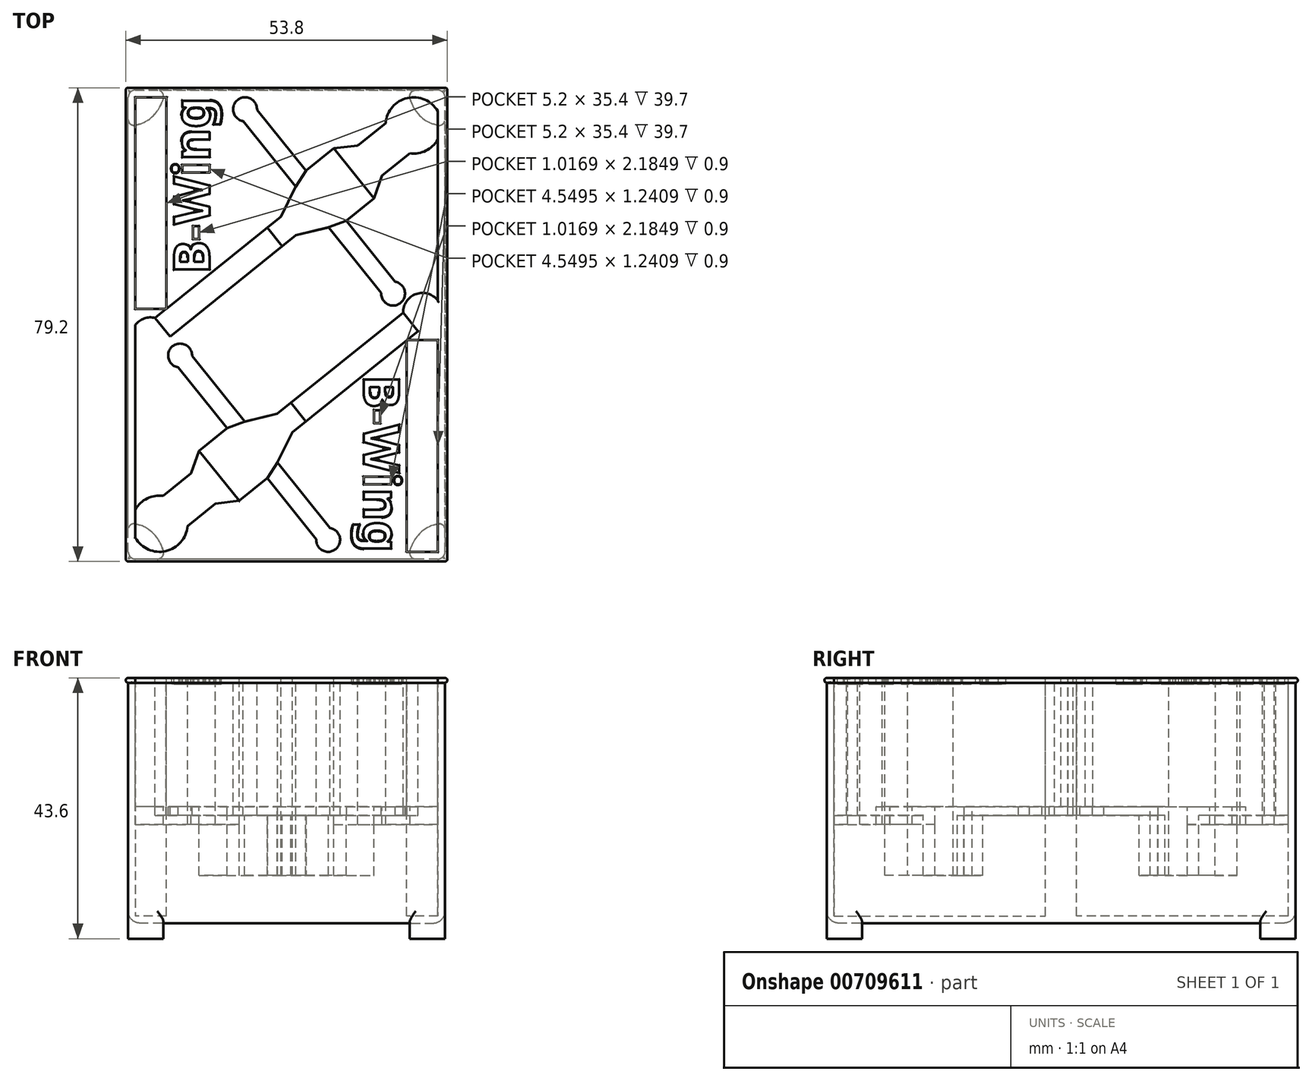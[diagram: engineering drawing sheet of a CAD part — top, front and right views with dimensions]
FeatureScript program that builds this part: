
annotation { "Feature Type Name" : "Feature", "Feature Type Description" : "" }
export const myFeature = defineFeature(function(context is Context, id is Id, definition is map)
    precondition{}
    {
        {
            var Q0;
            Q0=qCreatedBy(makeId("Front.planeOp"),FACE);
            var sketch = newSketch(context, id + "F0", { "sketchPlane" : qUnion([Q0])});
            skLineSegment(sketch, "E0.bottom", {"start": v(26.5, 20.5) * mm, "end": v(-26.5, 20.5) * mm});
            skLineSegment(sketch, "E0.top", {"start": v(26.5, -20.5) * mm, "end": v(-26.5, -20.5) * mm});
            skLineSegment(sketch, "E0.left", {"start": v(26.5, 20.5) * mm, "end": v(26.5, -20.5) * mm});
            skLineSegment(sketch, "E0.right", {"start": v(-26.5, 20.5) * mm, "end": v(-26.5, -20.5) * mm});
            skPoint(sketch, "E0.middle", {"position": v(0, 0) * mm});
            skSolve(sketch);
        }
        {
            var Q0;
            Q0=makeQuery(id+"F0.imprint","IMPRINT",FACE,{"disambiguationData":[TD([[makeQuery(id+"F0.imprint","IMPRINT",EDGE,{"derivedFrom":sQuery(id+"F0.wireOp",EDGE,"E0.bottom")}),1.0]])]});
            extrude(context, id + "F1", {"entities" : qUnion([Q0]), "depth" : 78.4 * mm, "offsetDistance" : 25 * mm, "symmetric" : true});
        }
        {
            var Q0;
            Q0=makeQuery(id+"F1.opExtrude","SWEPT_FACE",FACE,{"disambiguationData":[OSD([sQuery(id+"F0.wireOp",EDGE,"E0.bottom")])]});
            shell(context, id + "F2", {"entities" : qUnion([Q0]), "thickness" : 1.2 * mm});
        }
        {
            var Q0;
            Q0=makeQuery(id+"F1.opExtrude","SWEPT_FACE",FACE,{"disambiguationData":[OSD([sQuery(id+"F0.wireOp",EDGE,"E0.top")])]});
            var sketch = newSketch(context, id + "F3", { "sketchPlane" : qUnion([Q0])});
            skArc(sketch, "E1", {"start": v(20.62, 38) * mm, "mid": v(22.26, 34.96) * mm, "end": v(25.3, 33.32) * mm});
            skLineSegment(sketch, "E2", {"start": v(26.5, 39.2) * mm, "end": v(21.6, 39.2) * mm});
            skLineSegment(sketch, "E3", {"start": v(26.5, 39.2) * mm, "end": v(26.5, 34.3) * mm});
            skPoint(sketch, "E4.visualSharp", {"position": v(20.5, 39.2) * mm});
            skArc(sketch, "E4.filletArc", {"start": v(21.6, 39.2) * mm, "mid": v(20.83, 38.83) * mm, "end": v(20.62, 38) * mm});
            skPoint(sketch, "E5.visualSharp", {"position": v(26.5, 33.2) * mm});
            skArc(sketch, "E5.filletArc", {"start": v(25.3, 33.32) * mm, "mid": v(26.13, 33.53) * mm, "end": v(26.5, 34.3) * mm});
            skArc(sketch, "E6.MirrorCS", {"start": v(-25.3, 33.32) * mm, "mid": v(-26.13, 33.53) * mm, "end": v(-26.5, 34.3) * mm});
            skArc(sketch, "E7.MirrorCS", {"start": v(-21.6, 39.2) * mm, "mid": v(-20.83, 38.83) * mm, "end": v(-20.62, 38) * mm});
            skPoint(sketch, "E8.MirrorP", {"position": v(-20.5, 39.2) * mm});
            skArc(sketch, "E9.MirrorCS", {"start": v(-20.62, 38) * mm, "mid": v(-22.26, 34.96) * mm, "end": v(-25.3, 33.32) * mm});
            skLineSegment(sketch, "E10.MirrorCS", {"start": v(-26.5, 39.2) * mm, "end": v(-21.6, 39.2) * mm});
            skLineSegment(sketch, "E11.MirrorCS", {"start": v(-26.5, 39.2) * mm, "end": v(-26.5, 34.3) * mm});
            skPoint(sketch, "E12.MirrorP", {"position": v(-26.5, 33.2) * mm});
            skArc(sketch, "E13.MirrorCS", {"start": v(25.3, -33.32) * mm, "mid": v(26.13, -33.53) * mm, "end": v(26.5, -34.3) * mm});
            skArc(sketch, "E14.MirrorCS", {"start": v(21.6, -39.2) * mm, "mid": v(20.83, -38.83) * mm, "end": v(20.62, -38) * mm});
            skArc(sketch, "E15.MirrorCS", {"start": v(-25.3, -33.32) * mm, "mid": v(-26.13, -33.53) * mm, "end": v(-26.5, -34.3) * mm});
            skArc(sketch, "E16.MirrorCS", {"start": v(-21.6, -39.2) * mm, "mid": v(-20.83, -38.83) * mm, "end": v(-20.62, -38) * mm});
            skPoint(sketch, "E17.MirrorP", {"position": v(-26.5, -33.2) * mm});
            skPoint(sketch, "E18.MirrorP", {"position": v(20.5, -39.2) * mm});
            skPoint(sketch, "E19.MirrorP", {"position": v(26.5, -33.2) * mm});
            skLineSegment(sketch, "E20.MirrorCS", {"start": v(-26.5, -39.2) * mm, "end": v(-26.5, -34.3) * mm});
            skPoint(sketch, "E21.MirrorP", {"position": v(-20.5, -39.2) * mm});
            skLineSegment(sketch, "E22.MirrorCS", {"start": v(26.5, -39.2) * mm, "end": v(26.5, -34.3) * mm});
            skLineSegment(sketch, "E23.MirrorCS", {"start": v(-26.5, -39.2) * mm, "end": v(-21.6, -39.2) * mm});
            skLineSegment(sketch, "E24.MirrorCS", {"start": v(26.5, -39.2) * mm, "end": v(21.6, -39.2) * mm});
            skArc(sketch, "E25.MirrorCS", {"start": v(20.62, -38) * mm, "mid": v(22.26, -34.96) * mm, "end": v(25.3, -33.32) * mm});
            skArc(sketch, "E26.MirrorCS", {"start": v(-20.62, -38) * mm, "mid": v(-22.26, -34.96) * mm, "end": v(-25.3, -33.32) * mm});
            skSolve(sketch);
        }
        {
            var Q0;
            Q0=qSketchRegion(id+"F3",true);
            extrude(context, id + "F4", {"entities" : qUnion([Q0]), "operationType" : NewBodyOperationType.ADD, "depth" : 2.6 * mm, "offsetDistance" : 25 * mm});
        }
        {
            var Q0;
            Q0=makeQuery(id+"F4.boolean.opBoolean","MERGE",FACE,{"derivedFrom":[makeQuery(id+"F1.opExtrude","CAP_FACE",FACE,{"disambiguationData":[OSD([sQuery(id+"F0.wireOp",EDGE,"E0.bottom"),sQuery(id+"F0.wireOp",EDGE,"E0.top"),sQuery(id+"F0.wireOp",EDGE,"E0.left"),sQuery(id+"F0.wireOp",EDGE,"E0.right")])],"isStart":false}),makeQuery(id+"F4.opExtrude","SWEPT_FACE",FACE,{"disambiguationData":[OSD([sQuery(id+"F3.wireOp",EDGE,"E2")])]}),makeQuery(id+"F4.opExtrude","SWEPT_FACE",FACE,{"disambiguationData":[OSD([sQuery(id+"F3.wireOp",EDGE,"E10.MirrorCS")])]})]});
            var sketch = newSketch(context, id + "F5", { "sketchPlane" : qUnion([Q0])});
            skLineSegment(sketch, "E27", {"start": v(-26.5, 20.5) * mm, "end": v(-26.5, 19.7) * mm});
            skArc(sketch, "E28", {"start": v(-26.5, 20.5) * mm, "mid": v(-26.9, 20.1) * mm, "end": v(-26.5, 19.7) * mm});
            skSolve(sketch);
        }
        {
            var Q0;
            Q0=makeQuery(id+"F5.imprint","IMPRINT",FACE,{"disambiguationData":[TD([[makeQuery(id+"F5.imprint","IMPRINT",EDGE,{"derivedFrom":sQuery(id+"F5.wireOp",EDGE,"E27")}),-1.0]])]});
            var Q1;
            Q1=makeQuery(id+"F1.opExtrude","SWEPT_EDGE",EDGE,{"disambiguationData":[OSD([sQuery(id+"F0.wireOp",EDGE,"E0.bottom"),sQuery(id+"F0.wireOp",EDGE,"E0.right")])]});
            var Q2;
            Q2=makeQuery(id+"F1.opExtrude","CAP_EDGE",EDGE,{"disambiguationData":[OSD([sQuery(id+"F0.wireOp",EDGE,"E0.bottom")])],"isStart":false});
            var Q3;
            Q3=makeQuery(id+"F1.opExtrude","SWEPT_EDGE",EDGE,{"disambiguationData":[OSD([sQuery(id+"F0.wireOp",EDGE,"E0.bottom"),sQuery(id+"F0.wireOp",EDGE,"E0.left")])]});
            var Q4;
            Q4=makeQuery(id+"F1.opExtrude","CAP_EDGE",EDGE,{"disambiguationData":[OSD([sQuery(id+"F0.wireOp",EDGE,"E0.bottom")])],"isStart":true});
            sweep(context, id + "F6", {"operationType" : NewBodyOperationType.ADD, "profiles" : qUnion([Q0]), "path" : qUnion([Q1, Q2, Q3, Q4])});
        }
        {
            var Q0;
            Q0=makeQuery(id+"F1.opExtrude","CAP_EDGE",EDGE,{"disambiguationData":[OSD([sQuery(id+"F0.wireOp",EDGE,"E0.top")])],"isStart":false});
            var Q1;
            Q1=makeQuery(id+"F1.opExtrude","SWEPT_EDGE",EDGE,{"disambiguationData":[OSD([sQuery(id+"F0.wireOp",EDGE,"E0.top"),sQuery(id+"F0.wireOp",EDGE,"E0.left")])]});
            var Q2;
            Q2=makeQuery(id+"F1.opExtrude","SWEPT_EDGE",EDGE,{"disambiguationData":[OSD([sQuery(id+"F0.wireOp",EDGE,"E0.top"),sQuery(id+"F0.wireOp",EDGE,"E0.right")])]});
            var Q3;
            Q3=makeQuery(id+"F1.opExtrude","CAP_EDGE",EDGE,{"disambiguationData":[OSD([sQuery(id+"F0.wireOp",EDGE,"E0.top")])],"isStart":true});
            fillet(context, id + "F7", {"entities" : qUnion([Q0, Q1, Q2, Q3]), "radius" : 2 * mm, "tangentPropagation" : true, "allowEdgeOverflow" : false});
        }
        {
            var Q0;
            Q0=makeQuery(id+"F4.boolean.opBoolean","MERGE",EDGE,{"derivedFrom":[makeQuery(id+"F1.opExtrude","CAP_EDGE",EDGE,{"disambiguationData":[OSD([sQuery(id+"F0.wireOp",EDGE,"E0.right")])],"isStart":false}),makeQuery(id+"F4.opExtrude","SWEPT_EDGE",EDGE,{"disambiguationData":[OSD([sQuery(id+"F3.wireOp",EDGE,"E10.MirrorCS"),sQuery(id+"F3.wireOp",EDGE,"E11.MirrorCS")])]})]});
            var Q1;
            Q1=makeQuery(id+"F4.boolean.opBoolean","MERGE",EDGE,{"derivedFrom":[makeQuery(id+"F1.opExtrude","CAP_EDGE",EDGE,{"disambiguationData":[OSD([sQuery(id+"F0.wireOp",EDGE,"E0.left")])],"isStart":false}),makeQuery(id+"F4.opExtrude","SWEPT_EDGE",EDGE,{"disambiguationData":[OSD([sQuery(id+"F3.wireOp",EDGE,"E2"),sQuery(id+"F3.wireOp",EDGE,"E3")])]})]});
            var Q2;
            Q2=makeQuery(id+"F4.boolean.opBoolean","MERGE",EDGE,{"derivedFrom":[makeQuery(id+"F1.opExtrude","CAP_EDGE",EDGE,{"disambiguationData":[OSD([sQuery(id+"F0.wireOp",EDGE,"E0.left")])],"isStart":true}),makeQuery(id+"F4.opExtrude","SWEPT_EDGE",EDGE,{"disambiguationData":[OSD([sQuery(id+"F3.wireOp",EDGE,"E22.MirrorCS"),sQuery(id+"F3.wireOp",EDGE,"E24.MirrorCS")])]})]});
            var Q3;
            Q3=makeQuery(id+"F4.boolean.opBoolean","MERGE",EDGE,{"derivedFrom":[makeQuery(id+"F1.opExtrude","CAP_EDGE",EDGE,{"disambiguationData":[OSD([sQuery(id+"F0.wireOp",EDGE,"E0.right")])],"isStart":true}),makeQuery(id+"F4.opExtrude","SWEPT_EDGE",EDGE,{"disambiguationData":[OSD([sQuery(id+"F3.wireOp",EDGE,"E20.MirrorCS"),sQuery(id+"F3.wireOp",EDGE,"E23.MirrorCS")])]})]});
            fillet(context, id + "F8", {"entities" : qUnion([Q0, Q1, Q2, Q3]), "radius" : 1.2 * mm, "tangentPropagation" : true, "allowEdgeOverflow" : false});
        }
        {
            var Q0;
            Q0=makeQuery(id+"F6.opSweep","MID_CAP_EDGE",EDGE,{"disambiguationData":[OSD([sQuery(id+"F0.wireOp",EDGE,"E0.bottom"),sQuery(id+"F0.wireOp",EDGE,"E0.right"),sQuery(id+"F5.wireOp",EDGE,"E28")])],"capPos":1.0});
            var Q1;
            Q1=makeQuery(id+"F6.opSweep","CAP_EDGE",EDGE,{"disambiguationData":[OSD([sQuery(id+"F0.wireOp",EDGE,"E0.bottom"),sQuery(id+"F0.wireOp",EDGE,"E0.right"),sQuery(id+"F5.wireOp",EDGE,"E28")])],"isStart":true});
            var Q2;
            Q2=makeQuery(id+"F6.opSweep","MID_CAP_EDGE",EDGE,{"disambiguationData":[OSD([sQuery(id+"F0.wireOp",EDGE,"E0.bottom"),sQuery(id+"F0.wireOp",EDGE,"E0.left"),sQuery(id+"F5.wireOp",EDGE,"E28")])],"capPos":3.0});
            var Q3;
            Q3=makeQuery(id+"F6.opSweep","MID_CAP_EDGE",EDGE,{"disambiguationData":[OSD([sQuery(id+"F0.wireOp",EDGE,"E0.bottom"),sQuery(id+"F0.wireOp",EDGE,"E0.left"),sQuery(id+"F5.wireOp",EDGE,"E28")])],"capPos":2.0});
            fillet(context, id + "F9", {"entities" : qUnion([Q0, Q1, Q2, Q3]), "radius" : .4 * mm, "tangentPropagation" : true, "allowEdgeOverflow" : false});
        }
        {
            var Q0;
            {var subQ0=sQuery(id+"F12.wireOp",EDGE,"E179.MirrorCS");var subQ1=sQuery(id+"F12.wireOp",EDGE,"E174.MirrorCS");var subQ2=sQuery(id+"F12.wireOp",EDGE,"E171.MirrorCS");var subQ3=sQuery(id+"F12.wireOp",EDGE,"E87");var subQ4=sQuery(id+"F12.wireOp",EDGE,"E86");var subQ5=sQuery(id+"F12.wireOp",EDGE,"E85.0");var subQ6=sQuery(id+"F12.wireOp",EDGE,"E83.MirrorCS");var subQ7=sQuery(id+"F12.wireOp",EDGE,"E76.MirrorCS");Q0=makeQuery(id+"F13.boolean.opBoolean","MERGE",FACE,{"derivedFrom":[makeQuery(id+"F1.opExtrude","SWEPT_FACE",FACE,{"disambiguationData":[OSD([sQuery(id+"F0.wireOp",EDGE,"E0.bottom")])]}),makeQuery(id+"F13.opExtrude","CAP_FACE",FACE,{"disambiguationData":[OSD([sQuery(id+"F12.wireOp",EDGE,"E64"),sQuery(id+"F12.wireOp",EDGE,"E65"),sQuery(id+"F12.wireOp",EDGE,"E66"),sQuery(id+"F12.wireOp",EDGE,"E67"),sQuery(id+"F12.wireOp",EDGE,"E68"),sQuery(id+"F12.wireOp",EDGE,"E69"),sQuery(id+"F12.wireOp",EDGE,"E70"),sQuery(id+"F12.wireOp",EDGE,"E71"),sQuery(id+"F12.wireOp",EDGE,"E72"),sQuery(id+"F12.wireOp",EDGE,"E73.trimOffspring"),sQuery(id+"F12.wireOp",EDGE,"E79.MirrorCS"),subQ4,subQ3,sQuery(id+"F12.wireOp",EDGE,"E161.MirrorCS"),sQuery(id+"F12.wireOp",EDGE,"E162.MirrorCS"),sQuery(id+"F12.wireOp",EDGE,"E163.MirrorCS"),sQuery(id+"F12.wireOp",EDGE,"E164.MirrorCS"),sQuery(id+"F12.wireOp",EDGE,"E168.MirrorCS"),sQuery(id+"F12.wireOp",EDGE,"E169.MirrorCS"),sQuery(id+"F12.wireOp",EDGE,"E170.MirrorCS"),sQuery(id+"F12.wireOp",EDGE,"E173.MirrorCS"),sQuery(id+"F12.wireOp",EDGE,"E177.MirrorCS"),sQuery(id+"F12.wireOp",EDGE,"E178.MirrorCS"),sQuery(id+"F12.wireOp",EDGE,"E182.MirrorCS")])],"isStart":true}),makeQuery(id+"F13.opExtrude","CAP_FACE",FACE,{"disambiguationData":[OSD([sQuery(id+"F12.wireOp",EDGE,"E74.MirrorCS"),sQuery(id+"F12.wireOp",EDGE,"E75.MirrorCS"),subQ7,sQuery(id+"F12.wireOp",EDGE,"E77.MirrorCS"),sQuery(id+"F12.wireOp",EDGE,"E82.MirrorCS"),subQ6,subQ5])],"isStart":true}),makeQuery(id+"F13.opExtrude","CAP_FACE",FACE,{"disambiguationData":[OSD([subQ7,subQ5,subQ4,sQuery(id+"F12.wireOp",EDGE,"E184.trimOffspring")])],"isStart":true}),makeQuery(id+"F13.opExtrude","CAP_FACE",FACE,{"disambiguationData":[OSD([sQuery(id+"F12.wireOp",EDGE,"E78.MirrorCS"),sQuery(id+"F12.wireOp",EDGE,"E80.MirrorCS"),sQuery(id+"F12.wireOp",EDGE,"E81.MirrorCS"),subQ6,subQ5,subQ3,sQuery(id+"F12.wireOp",EDGE,"E186.trimOffspring")])],"isStart":true}),makeQuery(id+"F13.opExtrude","CAP_FACE",FACE,{"disambiguationData":[OSD([subQ4,sQuery(id+"F12.wireOp",EDGE,"E167.MirrorCS"),subQ2,sQuery(id+"F12.wireOp",EDGE,"E175.MirrorCS"),subQ0,sQuery(id+"F12.wireOp",EDGE,"E181.MirrorCS"),sQuery(id+"F12.wireOp",EDGE,"E185.trimOffspring")])],"isStart":true}),makeQuery(id+"F13.opExtrude","CAP_FACE",FACE,{"disambiguationData":[OSD([subQ3,subQ1,subQ0,sQuery(id+"F12.wireOp",EDGE,"E187.trimOffspring")])],"isStart":true}),makeQuery(id+"F13.opExtrude","CAP_FACE",FACE,{"disambiguationData":[OSD([sQuery(id+"F12.wireOp",EDGE,"E165.MirrorCS"),sQuery(id+"F12.wireOp",EDGE,"E166.MirrorCS"),subQ2,sQuery(id+"F12.wireOp",EDGE,"E172.MirrorCS"),subQ1,sQuery(id+"F12.wireOp",EDGE,"E176.MirrorCS"),subQ0])],"isStart":true})]});}
            var sketch = newSketch(context, id + "F10", { "sketchPlane" : qUnion([Q0])});
            skLineSegment(sketch, "E29.0", {"start": v(38.64, -19.37) * mm, "end": v(38.64, 56.63) * mm});
            skLineSegment(sketch, "E30.MirrorCS", {"start": v(48.84, -19.37) * mm, "end": v(48.84, 16.03) * mm});
            skLineSegment(sketch, "E31.MirrorCS", {"start": v(48.84, 16.03) * mm, "end": v(38.64, 16.03) * mm});
            skLineSegment(sketch, "E32", {"start": v(25.3, -38) * mm, "end": v(25.3, -2.6) * mm});
            skLineSegment(sketch, "E33", {"start": v(25.3, -2.6) * mm, "end": v(20.1, -2.6) * mm});
            skLineSegment(sketch, "E34", {"start": v(20.1, -2.6) * mm, "end": v(20.1, -38) * mm});
            skLineSegment(sketch, "E35", {"start": v(20.1, -38) * mm, "end": v(25.3, -38) * mm});
            skLineSegment(sketch, "E36", {"start": v(-25.3, 38) * mm, "end": v(-20.1, 38) * mm});
            skLineSegment(sketch, "E37", {"start": v(-20.1, 38) * mm, "end": v(-20.1, 2.6) * mm});
            skLineSegment(sketch, "E38", {"start": v(-20.1, 2.6) * mm, "end": v(-25.3, 2.6) * mm});
            skLineSegment(sketch, "E39", {"start": v(-25.3, 2.6) * mm, "end": v(-25.3, 38) * mm});
            skSolve(sketch);
        }
        {
            var Q0;
            {var subQ3=sQuery(id+"F10.wireOp",EDGE,"E33");Q0=makeQuery(id+"F10.imprint","IMPRINT",FACE,{"disambiguationData":[TD([[makeQuery(id+"F10.imprint","IMPRINT",EDGE,{"derivedFrom":subQ3}),-1.0]])]});}
            var Q1;
            Q1=makeQuery(id+"F13.boolean.opBoolean","SPLIT",FACE,{"disambiguationData":[TD([makeQuery(id+"F13.opExtrude","SWEPT_FACE",FACE,{"disambiguationData":[OSD([sQuery(id+"F12.wireOp",EDGE,"E64")])]})])],"derivedFrom":makeQuery(id+"F2.opShell","OFFSET_FACE",FACE,{"disambiguationData":[OSD([sQuery(id+"F0.wireOp",EDGE,"E0.top")])]})});
            extrude(context, id + "F11", {"entities" : qUnion([Q0]), "operationType" : NewBodyOperationType.ADD, "endBound" : BoundingType.UP_TO_SURFACE, "oppositeDirection" : true, "depth" : 25 * mm, "endBoundEntityFace" : qUnion([Q1]), "offsetDistance" : 25 * mm});
        }
        {
            var Q0;
            Q0=makeQuery(id+"F1.opExtrude","SWEPT_FACE",FACE,{"disambiguationData":[OSD([sQuery(id+"F0.wireOp",EDGE,"E0.bottom")])]});
            var sketch = newSketch(context, id + "F12", { "sketchPlane" : qUnion([Q0])});
            skLineSegment(sketch, "E40", {"start": v(240.04, 16.27) * mm, "end": v(253.11, 16.27) * mm});
            skLineSegment(sketch, "E41", {"start": v(240.04, 16.27) * mm, "end": v(240.04, 22.27) * mm});
            skLineSegment(sketch, "E42", {"start": v(236.67, 8.2) * mm, "end": v(236.67, -18.8) * mm});
            skLineSegment(sketch, "E43", {"start": v(237.92, 25.66) * mm, "end": v(237.92, 31.66) * mm});
            skLineSegment(sketch, "E44", {"start": v(239.04, 13.27) * mm, "end": v(236.67, 8.2) * mm});
            skLineSegment(sketch, "E45", {"start": v(240.04, 22.27) * mm, "end": v(237.92, 25.66) * mm});
            skArc(sketch, "E46", {"start": v(234.67, -24.62) * mm, "mid": v(237.74, -22.43) * mm, "end": v(236.67, -18.8) * mm});
            skArc(sketch, "E47", {"start": v(237.92, 31.66) * mm, "mid": v(239.03, 36.8) * mm, "end": v(234.67, 39.76) * mm});
            skArc(sketch, "E48", {"start": v(253.11, 13.27) * mm, "mid": v(256.44, 14.77) * mm, "end": v(253.11, 16.27) * mm});
            skLineSegment(sketch, "E49.trimOffspring", {"start": v(253.11, 13.27) * mm, "end": v(239.04, 13.27) * mm});
            skPoint(sketch, "E50.orphan", {"position": v(237.87, -18.8) * mm});
            skPoint(sketch, "E51.start.orphan", {"position": v(237.92, 28.66) * mm});
            skLineSegment(sketch, "E52.MirrorCS", {"start": v(229.3, 22.27) * mm, "end": v(231.42, 25.66) * mm});
            skLineSegment(sketch, "E53.MirrorCS", {"start": v(231.42, 25.66) * mm, "end": v(231.42, 31.66) * mm});
            skArc(sketch, "E54.MirrorCS", {"start": v(231.42, 31.66) * mm, "mid": v(230.3, 36.8) * mm, "end": v(234.67, 39.76) * mm});
            skLineSegment(sketch, "E55.MirrorCS", {"start": v(229.3, 16.27) * mm, "end": v(229.3, 22.27) * mm});
            skLineSegment(sketch, "E56.MirrorCS", {"start": v(216.22, 13.27) * mm, "end": v(230.3, 13.27) * mm});
            skArc(sketch, "E57.MirrorCS", {"start": v(234.67, -24.62) * mm, "mid": v(231.6, -22.43) * mm, "end": v(232.67, -18.8) * mm});
            skLineSegment(sketch, "E58.MirrorCS", {"start": v(230.3, 13.27) * mm, "end": v(232.67, 8.2) * mm});
            skLineSegment(sketch, "E59.MirrorCS", {"start": v(232.67, 8.2) * mm, "end": v(232.67, -18.8) * mm});
            skPoint(sketch, "E60.MirrorP", {"position": v(231.47, -18.8) * mm});
            skLineSegment(sketch, "E61.MirrorCS", {"start": v(229.3, 16.27) * mm, "end": v(216.22, 16.27) * mm});
            skArc(sketch, "E62.MirrorCS", {"start": v(216.22, 13.27) * mm, "mid": v(212.9, 14.77) * mm, "end": v(216.22, 16.27) * mm});
            skPoint(sketch, "E63.MirrorP", {"position": v(231.42, 28.66) * mm});
            skLineSegment(sketch, "E64", {"start": v(9.97, 17.35) * mm, "end": v(18.16, 7.15) * mm});
            skLineSegment(sketch, "E65", {"start": v(9.97, 17.35) * mm, "end": v(14.64, 21.1) * mm});
            skLineSegment(sketch, "E66", {"start": v(1.56, 14.91) * mm, "end": v(-19.49, -2) * mm});
            skLineSegment(sketch, "E67", {"start": v(15.96, 24.88) * mm, "end": v(20.63, 28.64) * mm});
            skLineSegment(sketch, "E68", {"start": v(7, 16.25) * mm, "end": v(1.56, 14.91) * mm});
            skLineSegment(sketch, "E69", {"start": v(14.64, 21.1) * mm, "end": v(15.96, 24.88) * mm});
            skArc(sketch, "E70", {"start": v(-25.27, -4.08) * mm, "mid": v(-21.64, -5.1) * mm, "end": v(-19.49, -2) * mm});
            skArc(sketch, "E71", {"start": v(20.63, 28.64) * mm, "mid": v(23.3, 29.08) * mm, "end": v(25.3, 30.92) * mm});
            skArc(sketch, "E72", {"start": v(15.82, 5.27) * mm, "mid": v(19.07, 3.62) * mm, "end": v(18.16, 7.15) * mm});
            skLineSegment(sketch, "E73.trimOffspring", {"start": v(15.82, 5.27) * mm, "end": v(7, 16.25) * mm});
            skLineSegment(sketch, "E74.MirrorCS", {"start": v(7.92, 29.47) * mm, "end": v(11.9, 29.94) * mm});
            skLineSegment(sketch, "E75.MirrorCS", {"start": v(11.9, 29.94) * mm, "end": v(16.57, 33.7) * mm});
            skArc(sketch, "E76.MirrorCS", {"start": v(16.57, 33.7) * mm, "mid": v(19.88, 37.8) * mm, "end": v(24.91, 36.24) * mm});
            skLineSegment(sketch, "E77.MirrorCS", {"start": v(3.24, 25.71) * mm, "end": v(7.92, 29.47) * mm});
            skLineSegment(sketch, "E78.MirrorCS", {"start": v(-7.29, 34.03) * mm, "end": v(1.53, 23.06) * mm});
            skArc(sketch, "E79.MirrorCS", {"start": v(-25.27, -4.08) * mm, "mid": v(-25.29, -4.06) * mm, "end": v(-25.3, -4.05) * mm});
            skLineSegment(sketch, "E80.MirrorCS", {"start": v(1.53, 23.06) * mm, "end": v(-0.95, 18.03) * mm});
            skLineSegment(sketch, "E81.MirrorCS", {"start": v(-0.95, 18.03) * mm, "end": v(-22, 1.12) * mm});
            skLineSegment(sketch, "E82.MirrorCS", {"start": v(3.24, 25.71) * mm, "end": v(-4.95, 35.9) * mm});
            skArc(sketch, "E83.MirrorCS", {"start": v(-7.29, 34.03) * mm, "mid": v(-8.2, 37.56) * mm, "end": v(-4.95, 35.9) * mm});
            skPoint(sketch, "E84.MirrorP", {"position": v(14.23, 31.82) * mm});
            skLineSegment(sketch, "E85.0", {"start": v(25.3, 38) * mm, "end": v(-25.3, 38) * mm});
            skLineSegment(sketch, "E85.1", {"start": v(-25.3, -38) * mm, "end": v(-25.3, 38) * mm});
            skLineSegment(sketch, "E85.2", {"start": v(25.3, -38) * mm, "end": v(25.3, 38) * mm});
            skLineSegment(sketch, "E85.3", {"start": v(25.3, -38) * mm, "end": v(-25.3, -38) * mm});
            skLineSegment(sketch, "E86", {"start": v(25.3, 38) * mm, "end": v(25.3, -38) * mm});
            skLineSegment(sketch, "E87", {"start": v(-25.3, 38) * mm, "end": v(-25.3, -38) * mm});
            skLineSegment(sketch, "E88", {"start": v(370.6, 14.54) * mm, "end": v(383.68, 14.54) * mm});
            skLineSegment(sketch, "E89", {"start": v(370.6, 14.54) * mm, "end": v(370.6, 20.54) * mm});
            skLineSegment(sketch, "E90", {"start": v(367.23, 6.46) * mm, "end": v(367.23, -20.54) * mm});
            skLineSegment(sketch, "E91", {"start": v(368.48, 23.93) * mm, "end": v(368.48, 29.93) * mm});
            skLineSegment(sketch, "E92", {"start": v(369.6, 11.54) * mm, "end": v(367.23, 6.46) * mm});
            skLineSegment(sketch, "E93", {"start": v(370.6, 20.54) * mm, "end": v(368.48, 23.93) * mm});
            skArc(sketch, "E94", {"start": v(365.23, -26.35) * mm, "mid": v(368.3, -24.16) * mm, "end": v(367.23, -20.54) * mm});
            skArc(sketch, "E95", {"start": v(368.48, 29.93) * mm, "mid": v(369.6, 35.08) * mm, "end": v(365.23, 38.03) * mm});
            skArc(sketch, "E96", {"start": v(383.68, 11.54) * mm, "mid": v(387, 13.04) * mm, "end": v(383.68, 14.54) * mm});
            skLineSegment(sketch, "E97.trimOffspring", {"start": v(383.68, 11.54) * mm, "end": v(369.6, 11.54) * mm});
            skLineSegment(sketch, "E98.MirrorCS", {"start": v(359.86, 20.54) * mm, "end": v(361.99, 23.93) * mm});
            skLineSegment(sketch, "E99.MirrorCS", {"start": v(361.99, 23.93) * mm, "end": v(361.99, 29.93) * mm});
            skArc(sketch, "E100.MirrorCS", {"start": v(361.99, 29.93) * mm, "mid": v(360.87, 35.08) * mm, "end": v(365.23, 38.03) * mm});
            skLineSegment(sketch, "E101.MirrorCS", {"start": v(359.86, 14.54) * mm, "end": v(359.86, 20.54) * mm});
            skLineSegment(sketch, "E102.MirrorCS", {"start": v(346.79, 11.54) * mm, "end": v(360.86, 11.54) * mm});
            skArc(sketch, "E103.MirrorCS", {"start": v(365.23, -26.35) * mm, "mid": v(362.16, -24.16) * mm, "end": v(363.23, -20.54) * mm});
            skLineSegment(sketch, "E104.MirrorCS", {"start": v(360.86, 11.54) * mm, "end": v(363.23, 6.46) * mm});
            skLineSegment(sketch, "E105.MirrorCS", {"start": v(363.23, 6.46) * mm, "end": v(363.23, -20.54) * mm});
            skLineSegment(sketch, "E106.MirrorCS", {"start": v(359.86, 14.54) * mm, "end": v(346.79, 14.54) * mm});
            skArc(sketch, "E107.MirrorCS", {"start": v(346.79, 11.54) * mm, "mid": v(343.46, 13.04) * mm, "end": v(346.79, 14.54) * mm});
            skPoint(sketch, "E108.MirrorP", {"position": v(361.99, 26.93) * mm});
            skLineSegment(sketch, "E109", {"start": v(364.1, 39.43) * mm, "end": v(332.41, -0.01) * mm});
            skLineSegment(sketch, "E110", {"start": v(364.1, 39.43) * mm, "end": v(423.35, -8.18) * mm});
            skLineSegment(sketch, "E111", {"start": v(332.41, -0.01) * mm, "end": v(391.65, -47.62) * mm});
            skLineSegment(sketch, "E112", {"start": v(423.35, -8.18) * mm, "end": v(332.5, -121.24) * mm});
            skArc(sketch, "E113.MirrorCS", {"start": v(451.14, -42.67) * mm, "mid": v(451.9, -39.1) * mm, "end": v(454.07, -42.03) * mm});
            skArc(sketch, "E114.MirrorCS", {"start": v(418.1, -68.84) * mm, "mid": v(420.91, -71.37) * mm, "end": v(424.22, -69.55) * mm});
            skArc(sketch, "E115.MirrorCS", {"start": v(418.1, -68.84) * mm, "mid": v(419.59, -65.37) * mm, "end": v(423.35, -65.64) * mm});
            skArc(sketch, "E116.MirrorCS", {"start": v(473.77, -59.9) * mm, "mid": v(479.04, -59.88) * mm, "end": v(480.98, -54.99) * mm});
            skArc(sketch, "E117.MirrorCS", {"start": v(459.08, -78.7) * mm, "mid": v(461.26, -81.62) * mm, "end": v(462.01, -78.05) * mm});
            skLineSegment(sketch, "E118.MirrorCS", {"start": v(466.51, -54.85) * mm, "end": v(472.37, -53.56) * mm});
            skLineSegment(sketch, "E119.MirrorCS", {"start": v(465.06, -64) * mm, "end": v(467.91, -61.2) * mm});
            skLineSegment(sketch, "E120.MirrorCS", {"start": v(456.89, -54.8) * mm, "end": v(462.74, -53.5) * mm});
            skArc(sketch, "E121.MirrorCS", {"start": v(472.37, -53.56) * mm, "mid": v(477.16, -51.36) * mm, "end": v(480.98, -54.99) * mm});
            skLineSegment(sketch, "E122.MirrorCS", {"start": v(462.74, -53.5) * mm, "end": v(466.51, -54.85) * mm});
            skLineSegment(sketch, "E123.MirrorCS", {"start": v(467.91, -61.2) * mm, "end": v(473.77, -59.9) * mm});
            skLineSegment(sketch, "E124.MirrorCS", {"start": v(456.05, -64.95) * mm, "end": v(450.58, -63.73) * mm});
            skLineSegment(sketch, "E125.MirrorCS", {"start": v(459.2, -65.28) * mm, "end": v(465.06, -64) * mm});
            skLineSegment(sketch, "E126.MirrorCS", {"start": v(454.17, -56.42) * mm, "end": v(449.72, -59.83) * mm});
            skLineSegment(sketch, "E127.MirrorCS", {"start": v(456.89, -54.8) * mm, "end": v(454.07, -42.03) * mm});
            skLineSegment(sketch, "E128.MirrorCS", {"start": v(451.14, -42.67) * mm, "end": v(454.17, -56.42) * mm});
            skLineSegment(sketch, "E129.MirrorCS", {"start": v(482.6, -55.78) * mm, "end": v(423.35, -8.18) * mm});
            skLineSegment(sketch, "E130.MirrorCS", {"start": v(459.08, -78.7) * mm, "end": v(456.05, -64.95) * mm});
            skPoint(sketch, "E131.MirrorP", {"position": v(470.84, -60.55) * mm});
            skLineSegment(sketch, "E132.MirrorCS", {"start": v(450.58, -63.73) * mm, "end": v(424.22, -69.55) * mm});
            skLineSegment(sketch, "E133.MirrorCS", {"start": v(459.2, -65.28) * mm, "end": v(462.01, -78.05) * mm});
            skLineSegment(sketch, "E134.MirrorCS", {"start": v(450.9, -95.23) * mm, "end": v(391.65, -47.62) * mm});
            skLineSegment(sketch, "E135.MirrorCS", {"start": v(482.6, -55.78) * mm, "end": v(450.9, -95.23) * mm});
            skLineSegment(sketch, "E136.MirrorCS", {"start": v(449.72, -59.83) * mm, "end": v(423.35, -65.64) * mm});
            skLineSegment(sketch, "E137", {"start": v(505.7, -35.8) * mm, "end": v(380, 65.2) * mm});
            skArc(sketch, "E138.MirrorCS", {"start": v(519.1, 56.84) * mm, "mid": v(522.18, 54.65) * mm, "end": v(521.1, 51.03) * mm});
            skArc(sketch, "E139.MirrorCS", {"start": v(519.1, 56.84) * mm, "mid": v(516.03, 54.65) * mm, "end": v(517.1, 51.03) * mm});
            skLineSegment(sketch, "E140.MirrorCS", {"start": v(515.86, 6.56) * mm, "end": v(515.86, 0.56) * mm});
            skLineSegment(sketch, "E141.MirrorCS", {"start": v(513.74, 9.95) * mm, "end": v(515.86, 6.56) * mm});
            skLineSegment(sketch, "E142.MirrorCS", {"start": v(524.47, 9.95) * mm, "end": v(522.35, 6.56) * mm});
            skLineSegment(sketch, "E143.MirrorCS", {"start": v(522.35, 6.56) * mm, "end": v(522.35, 0.56) * mm});
            skLineSegment(sketch, "E144.MirrorCS", {"start": v(523.47, 18.95) * mm, "end": v(521.1, 24.03) * mm});
            skLineSegment(sketch, "E145.MirrorCS", {"start": v(513.74, 15.95) * mm, "end": v(513.74, 9.95) * mm});
            skArc(sketch, "E146.MirrorCS", {"start": v(500.66, 18.95) * mm, "mid": v(497.34, 17.45) * mm, "end": v(500.66, 15.95) * mm});
            skArc(sketch, "E147.MirrorCS", {"start": v(515.86, 0.56) * mm, "mid": v(514.74, -4.6) * mm, "end": v(519.1, -7.54) * mm});
            skArc(sketch, "E148.MirrorCS", {"start": v(537.55, 18.95) * mm, "mid": v(540.87, 17.45) * mm, "end": v(537.55, 15.95) * mm});
            skLineSegment(sketch, "E149.MirrorCS", {"start": v(524.47, 15.95) * mm, "end": v(524.47, 9.95) * mm});
            skLineSegment(sketch, "E150.MirrorCS", {"start": v(514.74, 18.95) * mm, "end": v(517.1, 24.03) * mm});
            skArc(sketch, "E151.MirrorCS", {"start": v(522.35, 0.56) * mm, "mid": v(523.47, -4.6) * mm, "end": v(519.1, -7.54) * mm});
            skLineSegment(sketch, "E152.MirrorCS", {"start": v(537.55, 18.95) * mm, "end": v(523.47, 18.95) * mm});
            skLineSegment(sketch, "E153.MirrorCS", {"start": v(524.47, 15.95) * mm, "end": v(537.55, 15.95) * mm});
            skLineSegment(sketch, "E154.MirrorCS", {"start": v(513.74, 15.95) * mm, "end": v(500.66, 15.95) * mm});
            skLineSegment(sketch, "E155.MirrorCS", {"start": v(500.66, 18.95) * mm, "end": v(514.74, 18.95) * mm});
            skLineSegment(sketch, "E156.MirrorCS", {"start": v(520.23, -8.94) * mm, "end": v(551.93, 30.5) * mm});
            skPoint(sketch, "E157.MirrorP", {"position": v(522.35, 3.56) * mm});
            skLineSegment(sketch, "E158.MirrorCS", {"start": v(521.1, 24.03) * mm, "end": v(521.1, 51.03) * mm});
            skLineSegment(sketch, "E159.MirrorCS", {"start": v(517.1, 24.03) * mm, "end": v(517.1, 51.03) * mm});
            skPoint(sketch, "E160", {"position": v(551.93, 30.5) * mm});
            skArc(sketch, "E161.MirrorCS", {"start": v(25.27, 4.08) * mm, "mid": v(25.29, 4.06) * mm, "end": v(25.3, 4.05) * mm});
            skArc(sketch, "E162.MirrorCS", {"start": v(25.27, 4.08) * mm, "mid": v(21.64, 5.1) * mm, "end": v(19.49, 2) * mm});
            skLineSegment(sketch, "E163.MirrorCS", {"start": v(-15.96, -24.88) * mm, "end": v(-20.63, -28.64) * mm});
            skLineSegment(sketch, "E164.MirrorCS", {"start": v(-14.64, -21.1) * mm, "end": v(-15.96, -24.88) * mm});
            skLineSegment(sketch, "E165.MirrorCS", {"start": v(-7.92, -29.47) * mm, "end": v(-11.9, -29.94) * mm});
            skLineSegment(sketch, "E166.MirrorCS", {"start": v(-11.9, -29.94) * mm, "end": v(-16.57, -33.7) * mm});
            skLineSegment(sketch, "E167.MirrorCS", {"start": v(-1.53, -23.06) * mm, "end": v(0.95, -18.03) * mm});
            skLineSegment(sketch, "E168.MirrorCS", {"start": v(-9.97, -17.35) * mm, "end": v(-14.64, -21.1) * mm});
            skArc(sketch, "E169.MirrorCS", {"start": v(-15.82, -5.27) * mm, "mid": v(-19.07, -3.62) * mm, "end": v(-18.16, -7.15) * mm});
            skArc(sketch, "E170.MirrorCS", {"start": v(-20.63, -28.64) * mm, "mid": v(-23.3, -29.08) * mm, "end": v(-25.3, -30.92) * mm});
            skArc(sketch, "E171.MirrorCS", {"start": v(7.29, -34.03) * mm, "mid": v(8.2, -37.56) * mm, "end": v(4.95, -35.9) * mm});
            skLineSegment(sketch, "E172.MirrorCS", {"start": v(-3.24, -25.71) * mm, "end": v(-7.92, -29.47) * mm});
            skLineSegment(sketch, "E173.MirrorCS", {"start": v(-7, -16.25) * mm, "end": v(-1.56, -14.91) * mm});
            skArc(sketch, "E174.MirrorCS", {"start": v(-16.57, -33.7) * mm, "mid": v(-19.88, -37.8) * mm, "end": v(-24.91, -36.24) * mm});
            skLineSegment(sketch, "E175.MirrorCS", {"start": v(7.29, -34.03) * mm, "end": v(-1.53, -23.06) * mm});
            skLineSegment(sketch, "E176.MirrorCS", {"start": v(-3.24, -25.71) * mm, "end": v(4.95, -35.9) * mm});
            skLineSegment(sketch, "E177.MirrorCS", {"start": v(-9.97, -17.35) * mm, "end": v(-18.16, -7.15) * mm});
            skLineSegment(sketch, "E178.MirrorCS", {"start": v(-15.82, -5.27) * mm, "end": v(-7, -16.25) * mm});
            skLineSegment(sketch, "E179.MirrorCS", {"start": v(-25.3, -38) * mm, "end": v(25.3, -38) * mm});
            skPoint(sketch, "E180.MirrorP", {"position": v(-14.23, -31.82) * mm});
            skLineSegment(sketch, "E181.MirrorCS", {"start": v(0.95, -18.03) * mm, "end": v(22, -1.12) * mm});
            skLineSegment(sketch, "E182.MirrorCS", {"start": v(-1.56, -14.91) * mm, "end": v(19.49, 2) * mm});
            skPoint(sketch, "E183", {"position": v(25.3, -38) * mm});
            skArc(sketch, "E184.trimOffspring", {"start": v(25.3, 35.68) * mm, "mid": v(25.12, 35.97) * mm, "end": v(24.91, 36.24) * mm});
            skArc(sketch, "E185.trimOffspring", {"start": v(25.3, 0.05) * mm, "mid": v(23.82, -1.02) * mm, "end": v(22, -1.12) * mm});
            skArc(sketch, "E186.trimOffspring", {"start": v(-25.3, -0.05) * mm, "mid": v(-23.82, 1.02) * mm, "end": v(-22, 1.12) * mm});
            skArc(sketch, "E187.trimOffspring", {"start": v(-25.3, -35.68) * mm, "mid": v(-25.12, -35.97) * mm, "end": v(-24.91, -36.24) * mm});
            skLineSegment(sketch, "E188", {"start": v(7.92, 29.47) * mm, "end": v(14.64, 21.1) * mm});
            skLineSegment(sketch, "E189", {"start": v(-22, 1.12) * mm, "end": v(-19.49, -2) * mm});
            skLineSegment(sketch, "E190", {"start": v(19.49, 2) * mm, "end": v(22, -1.12) * mm});
            skLineSegment(sketch, "E191", {"start": v(-14.64, -21.1) * mm, "end": v(-7.92, -29.47) * mm});
            skLineSegment(sketch, "E192", {"start": v(-1.97, 14.64) * mm, "end": v(-0.72, 13.08) * mm});
            skLineSegment(sketch, "E193", {"start": v(-0.72, 13.08) * mm, "end": v(-3.22, 16.2) * mm});
            skLineSegment(sketch, "E194", {"start": v(1.97, -14.64) * mm, "end": v(3.22, -16.2) * mm});
            skLineSegment(sketch, "E195", {"start": v(3.22, -16.2) * mm, "end": v(0.72, -13.08) * mm});
            skLineSegment(sketch, "E196", {"start": v(-9.97, -17.35) * mm, "end": v(-7, -16.25) * mm});
            skLineSegment(sketch, "E197", {"start": v(-1.53, -23.06) * mm, "end": v(-3.24, -25.71) * mm});
            skLineSegment(sketch, "E198", {"start": v(3.24, 25.71) * mm, "end": v(1.53, 23.06) * mm});
            skLineSegment(sketch, "E199", {"start": v(9.97, 17.35) * mm, "end": v(7, 16.25) * mm});
            skSolve(sketch);
        }
        {
            var Q0;
            Q0=makeQuery(id+"F12.imprint","IMPRINT",FACE,{"disambiguationData":[TD([[makeQuery(id+"F12.imprint","IMPRINT",EDGE,{"derivedFrom":sQuery(id+"F12.wireOp",EDGE,"E65")}),1.0]])]});
            var Q1;
            {var subQ5=sQuery(id+"F12.wireOp",EDGE,"E167.MirrorCS");Q1=makeQuery(id+"F12.imprint","IMPRINT",FACE,{"disambiguationData":[TD([[makeQuery(id+"F12.imprint","IMPRINT",EDGE,{"derivedFrom":subQ5}),1.0]])]});}
            var Q2;
            Q2=makeQuery(id+"F2.opShell","OFFSET_FACE",FACE,{"disambiguationData":[OSD([sQuery(id+"F0.wireOp",EDGE,"E0.top")])]});
            extrude(context, id + "F13", {"entities" : qUnion([Q0, Q1]), "operationType" : NewBodyOperationType.REMOVE, "oppositeDirection" : true, "depth" : 33 * mm, "endBoundEntityFace" : qUnion([Q2]), "offsetDistance" : 25 * mm});
        }
        {
            var Q0;
            Q0=makeQuery(id+"F12.imprint","IMPRINT",FACE,{"disambiguationData":[TD([[makeQuery(id+"F12.imprint","IMPRINT",EDGE,{"derivedFrom":sQuery(id+"F12.wireOp",EDGE,"E67")}),1.0]])]});
            var Q1;
            Q1=makeQuery(id+"F12.imprint","IMPRINT",FACE,{"disambiguationData":[TD([[makeQuery(id+"F12.imprint","IMPRINT",EDGE,{"derivedFrom":sQuery(id+"F12.wireOp",EDGE,"E163.MirrorCS")}),1.0]])]});
            extrude(context, id + "F14", {"entities" : qUnion([Q0, Q1]), "operationType" : NewBodyOperationType.REMOVE, "oppositeDirection" : true, "depth" : 24.5 * mm, "offsetDistance" : 25 * mm});
        }
        {
            var Q0;
            Q0=makeQuery(id+"F12.imprint","IMPRINT",FACE,{"disambiguationData":[TD([[makeQuery(id+"F12.imprint","IMPRINT",EDGE,{"derivedFrom":sQuery(id+"F12.wireOp",EDGE,"E70")}),1.0]])]});
            var Q1;
            {var subQ1=sQuery(id+"F12.wireOp",EDGE,"E161.MirrorCS");Q1=makeQuery(id+"F12.imprint","IMPRINT",FACE,{"disambiguationData":[TD([[makeQuery(id+"F12.imprint","IMPRINT",EDGE,{"derivedFrom":subQ1}),-1.0]])]});}
            extrude(context, id + "F15", {"entities" : qUnion([Q0, Q1]), "operationType" : NewBodyOperationType.REMOVE, "oppositeDirection" : true, "depth" : 21.5 * mm, "offsetDistance" : 25 * mm});
        }
        {
            var Q0;
            {var subQ3=sQuery(id+"F12.wireOp",EDGE,"E78.MirrorCS");Q0=makeQuery(id+"F12.imprint","IMPRINT",FACE,{"disambiguationData":[TD([[makeQuery(id+"F12.imprint","IMPRINT",EDGE,{"derivedFrom":subQ3}),1.0]])]});}
            var Q1;
            Q1=makeQuery(id+"F12.imprint","IMPRINT",FACE,{"disambiguationData":[TD([[makeQuery(id+"F12.imprint","IMPRINT",EDGE,{"derivedFrom":sQuery(id+"F12.wireOp",EDGE,"E64")}),-1.0]])]});
            var Q2;
            {var subQ0=sQuery(id+"F12.wireOp",EDGE,"E189");Q2=makeQuery(id+"F12.imprint","IMPRINT",FACE,{"disambiguationData":[TD([[makeQuery(id+"F12.imprint","IMPRINT",EDGE,{"derivedFrom":subQ0}),1.0]])]});}
            var Q3;
            Q3=makeQuery(id+"F12.imprint","IMPRINT",FACE,{"disambiguationData":[TD([[makeQuery(id+"F12.imprint","IMPRINT",EDGE,{"derivedFrom":sQuery(id+"F12.wireOp",EDGE,"E169.MirrorCS")}),1.0]])]});
            var Q4;
            {var subQ1=sQuery(id+"F12.wireOp",EDGE,"E175.MirrorCS");Q4=makeQuery(id+"F12.imprint","IMPRINT",FACE,{"disambiguationData":[TD([[makeQuery(id+"F12.imprint","IMPRINT",EDGE,{"derivedFrom":subQ1}),1.0]])]});}
            var Q5;
            {var subQ0=sQuery(id+"F12.wireOp",EDGE,"E190");Q5=makeQuery(id+"F12.imprint","IMPRINT",FACE,{"disambiguationData":[TD([[makeQuery(id+"F12.imprint","IMPRINT",EDGE,{"derivedFrom":subQ0}),-1.0]])]});}
            extrude(context, id + "F16", {"entities" : qUnion([Q0, Q1, Q2, Q3, Q4, Q5]), "operationType" : NewBodyOperationType.REMOVE, "oppositeDirection" : true, "depth" : 23 * mm, "offsetDistance" : 25 * mm});
        }
        {
            var Q0;
            {var subQ0=sQuery(id+"F0.wireOp",EDGE,"E0.bottom");Q0=makeQuery(id+"F11.boolean.opBoolean","MERGE",FACE,{"derivedFrom":[makeQuery(id+"F1.opExtrude","SWEPT_FACE",FACE,{"disambiguationData":[OSD([subQ0])]}),makeQuery(id+"F11.opExtrude","CAP_FACE",FACE,{"disambiguationData":[OSD([subQ0,sQuery(id+"F0.wireOp",EDGE,"E0.left"),sQuery(id+"F0.wireOp",EDGE,"E0.right"),sQuery(id+"F10.wireOp",EDGE,"E33"),sQuery(id+"F10.wireOp",EDGE,"E34"),sQuery(id+"F10.wireOp",EDGE,"E37"),sQuery(id+"F10.wireOp",EDGE,"E38")])],"isStart":true})]});}
            var sketch = newSketch(context, id + "F17", { "sketchPlane" : qUnion([Q0])});
            skText(sketch, "E200", { "text": "B-Wing", "fontName": "NotoSans-Bold.ttf"});
            skLineSegment(sketch, "E201", {"start": v(-20.1, 8.46) * mm, "end": v(-18.9, 8.46) * mm});
            skLineSegment(sketch, "E202", {"start": v(-18.9, 39.2) * mm, "end": v(-18.9, 38) * mm});
            skLineSegment(sketch, "E203", {"start": v(-26.5, 0) * mm, "end": v(33.13, 0) * mm});
            skLineSegment(sketch, "E204", {"start": v(0, 39.2) * mm, "end": v(0, -56.25) * mm});
            skLineSegment(sketch, "E205.MirrorCS", {"start": v(20.1, -8.46) * mm, "end": v(18.9, -8.46) * mm});
            skLineSegment(sketch, "E206.MirrorCS", {"start": v(18.9, -39.2) * mm, "end": v(18.9, -38) * mm});
            skText(sketch, "E207", { "text": "B-Wing", "fontName": "NotoSans-Bold.ttf"});
            skLineSegment(sketch, "E208", {"start": v(-18.9, 39.2) * mm, "end": v(-26.5, 39.2) * mm});
            const initialGuessF17  = {"E200": [-0.0129, 0.00846, 0, 1, 0.006], "E207": [0.0129, -0.00846, 0, -1, 0.006]};
            skSetInitialGuess(sketch, initialGuessF17);
            skSolve(sketch);
        }
        {
            var Q0;
            Q0=makeQuery(id+"F17.imprint","IMPRINT",FACE,{"disambiguationData":[TD([[makeQuery(id+"F17.imprint","IMPRINT",EDGE,{"derivedFrom":sQuery(id+"F17.wireOp",EDGE,"E200.sketch_text.stroke-0")}),1.0]])]});
            var sketch = newSketch(context, id + "F18", { "sketchPlane" : qUnion([Q0])});
            skCircle(sketch, "E209", {"center": v(0, 0) * mm, "radius": 7 * mm});
            skPoint(sketch, "E209.first.point", {"position": v(-7, 0) * mm});
            skLineSegment(sketch, "E210", {"start": v(-6.4, 0) * mm, "end": v(-5.04, 1.18) * mm});
            skLineSegment(sketch, "E211", {"start": v(-5.04, 1.18) * mm, "end": v(-4.36, 0.76) * mm});
            skLineSegment(sketch, "E212", {"start": v(-4.36, 0.76) * mm, "end": v(-3.18, 0.58) * mm});
            skLineSegment(sketch, "E213", {"start": v(-3.18, 0.58) * mm, "end": v(-3.82, 1.05) * mm});
            skLineSegment(sketch, "E214", {"start": v(-3.82, 1.05) * mm, "end": v(-4.46, 1.82) * mm});
            skLineSegment(sketch, "E215", {"start": v(-4.46, 1.82) * mm, "end": v(-3.69, 2.46) * mm});
            skLineSegment(sketch, "E216", {"start": v(-3.69, 2.46) * mm, "end": v(-2.93, 1.53) * mm});
            skLineSegment(sketch, "E217", {"start": v(-2.93, 1.53) * mm, "end": v(-2.25, 1.1) * mm});
            skLineSegment(sketch, "E218", {"start": v(-2.25, 1.1) * mm, "end": v(-1.5, 0.84) * mm});
            skLineSegment(sketch, "E219", {"start": v(-1.5, 0.84) * mm, "end": v(-0.7, 0.84) * mm});
            skLineSegment(sketch, "E220", {"start": v(-0.7, 0.84) * mm, "end": v(0.06, 1.09) * mm});
            skLineSegment(sketch, "E221", {"start": v(0.06, 1.09) * mm, "end": v(0.73, 1.53) * mm});
            skLineSegment(sketch, "E222", {"start": v(0.73, 1.53) * mm, "end": v(1.14, 2.22) * mm});
            skLineSegment(sketch, "E223", {"start": v(1.14, 2.22) * mm, "end": v(1.14, 3.02) * mm});
            skLineSegment(sketch, "E224", {"start": v(1.14, 3.02) * mm, "end": v(0.79, 3.74) * mm});
            skLineSegment(sketch, "E225", {"start": v(0.79, 3.74) * mm, "end": v(0.18, 4.27) * mm});
            skLineSegment(sketch, "E226", {"start": v(0.18, 4.27) * mm, "end": v(-0.93, 4.72) * mm});
            skLineSegment(sketch, "E227", {"start": v(-0.93, 4.72) * mm, "end": v(-1.93, 4.72) * mm});
            skLineSegment(sketch, "E228", {"start": v(-1.93, 4.72) * mm, "end": v(-3.09, 4.4) * mm});
            skLineSegment(sketch, "E229", {"start": v(-3.09, 4.4) * mm, "end": v(-3.84, 4.13) * mm});
            skLineSegment(sketch, "E230", {"start": v(-3.84, 4.13) * mm, "end": v(-4.9, 3.56) * mm});
            skLineSegment(sketch, "E231", {"start": v(-4.9, 3.56) * mm, "end": v(-5.04, 3.42) * mm});
            skPoint(sketch, "E232", {"position": v(7, 0) * mm});
            skLineSegment(sketch, "E233.MirrorCS", {"start": v(-4.9, -3.56) * mm, "end": v(-5.04, -3.42) * mm});
            skLineSegment(sketch, "E234.MirrorCS", {"start": v(-4.46, -1.82) * mm, "end": v(-3.69, -2.46) * mm});
            skLineSegment(sketch, "E235.MirrorCS", {"start": v(-5.04, -1.18) * mm, "end": v(-4.36, -0.76) * mm});
            skLineSegment(sketch, "E236.MirrorCS", {"start": v(-0.93, -4.72) * mm, "end": v(-1.93, -4.72) * mm});
            skLineSegment(sketch, "E237.MirrorCS", {"start": v(-3.82, -1.05) * mm, "end": v(-4.46, -1.82) * mm});
            skLineSegment(sketch, "E238.MirrorCS", {"start": v(-2.25, -1.1) * mm, "end": v(-1.5, -0.84) * mm});
            skLineSegment(sketch, "E239.MirrorCS", {"start": v(0.06, -1.09) * mm, "end": v(0.73, -1.53) * mm});
            skLineSegment(sketch, "E240.MirrorCS", {"start": v(-3.69, -2.46) * mm, "end": v(-2.93, -1.53) * mm});
            skLineSegment(sketch, "E241.MirrorCS", {"start": v(1.14, -2.22) * mm, "end": v(1.14, -3.02) * mm});
            skLineSegment(sketch, "E242.MirrorCS", {"start": v(-0.7, -0.84) * mm, "end": v(0.06, -1.09) * mm});
            skLineSegment(sketch, "E243.MirrorCS", {"start": v(0.79, -3.74) * mm, "end": v(0.18, -4.27) * mm});
            skLineSegment(sketch, "E244.MirrorCS", {"start": v(-3.18, -0.58) * mm, "end": v(-3.82, -1.05) * mm});
            skLineSegment(sketch, "E245.MirrorCS", {"start": v(1.14, -3.02) * mm, "end": v(0.79, -3.74) * mm});
            skLineSegment(sketch, "E246.MirrorCS", {"start": v(0.73, -1.53) * mm, "end": v(1.14, -2.22) * mm});
            skLineSegment(sketch, "E247.MirrorCS", {"start": v(-2.93, -1.53) * mm, "end": v(-2.25, -1.1) * mm});
            skLineSegment(sketch, "E248.MirrorCS", {"start": v(-3.84, -4.13) * mm, "end": v(-4.9, -3.56) * mm});
            skLineSegment(sketch, "E249.MirrorCS", {"start": v(0.18, -4.27) * mm, "end": v(-0.93, -4.72) * mm});
            skLineSegment(sketch, "E250.MirrorCS", {"start": v(-1.5, -0.84) * mm, "end": v(-0.7, -0.84) * mm});
            skLineSegment(sketch, "E251.MirrorCS", {"start": v(-3.09, -4.4) * mm, "end": v(-3.84, -4.13) * mm});
            skLineSegment(sketch, "E252.MirrorCS", {"start": v(-1.93, -4.72) * mm, "end": v(-3.09, -4.4) * mm});
            skLineSegment(sketch, "E253.MirrorCS", {"start": v(-4.36, -0.76) * mm, "end": v(-3.18, -0.58) * mm});
            skLineSegment(sketch, "E254.MirrorCS", {"start": v(-6.4, 0) * mm, "end": v(-5.04, -1.18) * mm});
            skArc(sketch, "E255", {"start": v(-5.04, -3.42) * mm, "mid": v(6.1, 0) * mm, "end": v(-5.04, 3.42) * mm});
            skLineSegment(sketch, "E256.0", {"start": v(-26.5, -39.2) * mm, "end": v(-26.5, 39.2) * mm});
            skLineSegment(sketch, "E257", {"start": v(-7, 0) * mm, "end": v(-26.5, 0) * mm});
            skSolve(sketch);
        }
        {
            var Q0;
            Q0 = qSketchRegion(id + "F17", true);
            var Q1;
            Q1=makeQuery(id+"F18.imprint","IMPRINT",FACE,{"disambiguationData":[TD([[makeQuery(id+"F18.imprint","IMPRINT",EDGE,{"derivedFrom":sQuery(id+"F18.wireOp",EDGE,"E209")}),1.0]])]});
            extrude(context, id + "F19", {"entities" : qUnion([Q0, Q1]), "operationType" : NewBodyOperationType.REMOVE, "oppositeDirection" : true, "depth" : 1 * mm, "offsetDistance" : 25 * mm});
        }
        {
            var Q0;
            {var subQ2=sQuery(id+"F0.wireOp",EDGE,"E0.left");var subQ3=sQuery(id+"F0.wireOp",EDGE,"E0.bottom");var subQ7=sQuery(id+"F0.wireOp",EDGE,"E0.right");var subQ8=sQuery(id+"F10.wireOp",EDGE,"E37");var subQ12=sQuery(id+"F10.wireOp",EDGE,"E33");var subQ14=sQuery(id+"F10.wireOp",EDGE,"E34");var subQ15=sQuery(id+"F10.wireOp",EDGE,"E38");Q0=makeQuery(id+"F19.boolean.opBoolean","SPLIT",FACE,{"disambiguationData":[TD([makeQuery(id+"F2.opShell","OFFSET_FACE",FACE,{"disambiguationData":[OSD([subQ2])]})])],"derivedFrom":makeQuery(id+"F11.boolean.opBoolean","MERGE",FACE,{"derivedFrom":[makeQuery(id+"F1.opExtrude","SWEPT_FACE",FACE,{"disambiguationData":[OSD([subQ3])]}),makeQuery(id+"F11.opExtrude","CAP_FACE",FACE,{"disambiguationData":[OSD([subQ3,subQ2,subQ7,subQ12,subQ14,subQ8,subQ15])],"isStart":true})]})});}
            var Q1;
            {var subQ0=sQuery(id+"F0.wireOp",EDGE,"E0.bottom");Q1=makeQuery(id+"F19.boolean.opBoolean","SPLIT",FACE,{"disambiguationData":[TD([makeQuery(id+"F19.opExtrude","SWEPT_FACE",FACE,{"disambiguationData":[OSD([sQuery(id+"F17.wireOp",EDGE,"E200.sketch_text.stroke-12")])]})])],"derivedFrom":makeQuery(id+"F11.boolean.opBoolean","MERGE",FACE,{"derivedFrom":[makeQuery(id+"F1.opExtrude","SWEPT_FACE",FACE,{"disambiguationData":[OSD([subQ0])]}),makeQuery(id+"F11.opExtrude","CAP_FACE",FACE,{"disambiguationData":[OSD([subQ0,sQuery(id+"F0.wireOp",EDGE,"E0.left"),sQuery(id+"F0.wireOp",EDGE,"E0.right"),sQuery(id+"F10.wireOp",EDGE,"E33"),sQuery(id+"F10.wireOp",EDGE,"E34"),sQuery(id+"F10.wireOp",EDGE,"E37"),sQuery(id+"F10.wireOp",EDGE,"E38")])],"isStart":true})]})});}
            var Q2;
            {var subQ0=sQuery(id+"F0.wireOp",EDGE,"E0.bottom");Q2=makeQuery(id+"F19.boolean.opBoolean","SPLIT",FACE,{"disambiguationData":[TD([makeQuery(id+"F19.opExtrude","SWEPT_FACE",FACE,{"disambiguationData":[OSD([sQuery(id+"F17.wireOp",EDGE,"E200.sketch_text.stroke-19")])]})])],"derivedFrom":makeQuery(id+"F11.boolean.opBoolean","MERGE",FACE,{"derivedFrom":[makeQuery(id+"F1.opExtrude","SWEPT_FACE",FACE,{"disambiguationData":[OSD([subQ0])]}),makeQuery(id+"F11.opExtrude","CAP_FACE",FACE,{"disambiguationData":[OSD([subQ0,sQuery(id+"F0.wireOp",EDGE,"E0.left"),sQuery(id+"F0.wireOp",EDGE,"E0.right"),sQuery(id+"F10.wireOp",EDGE,"E33"),sQuery(id+"F10.wireOp",EDGE,"E34"),sQuery(id+"F10.wireOp",EDGE,"E37"),sQuery(id+"F10.wireOp",EDGE,"E38")])],"isStart":true})]})});}
            var Q3;
            {var subQ0=sQuery(id+"F0.wireOp",EDGE,"E0.bottom");Q3=makeQuery(id+"F19.boolean.opBoolean","SPLIT",FACE,{"disambiguationData":[TD([makeQuery(id+"F19.opExtrude","SWEPT_FACE",FACE,{"disambiguationData":[OSD([sQuery(id+"F17.wireOp",EDGE,"E200.sketch_text.stroke-79")])]})])],"derivedFrom":makeQuery(id+"F11.boolean.opBoolean","MERGE",FACE,{"derivedFrom":[makeQuery(id+"F1.opExtrude","SWEPT_FACE",FACE,{"disambiguationData":[OSD([subQ0])]}),makeQuery(id+"F11.opExtrude","CAP_FACE",FACE,{"disambiguationData":[OSD([subQ0,sQuery(id+"F0.wireOp",EDGE,"E0.left"),sQuery(id+"F0.wireOp",EDGE,"E0.right"),sQuery(id+"F10.wireOp",EDGE,"E33"),sQuery(id+"F10.wireOp",EDGE,"E34"),sQuery(id+"F10.wireOp",EDGE,"E37"),sQuery(id+"F10.wireOp",EDGE,"E38")])],"isStart":true})]})});}
            var Q4;
            {var subQ0=sQuery(id+"F0.wireOp",EDGE,"E0.bottom");Q4=makeQuery(id+"F19.boolean.opBoolean","SPLIT",FACE,{"disambiguationData":[TD([makeQuery(id+"F19.opExtrude","SWEPT_FACE",FACE,{"disambiguationData":[OSD([sQuery(id+"F17.wireOp",EDGE,"E207.sketch_text.stroke-19")])]})])],"derivedFrom":makeQuery(id+"F11.boolean.opBoolean","MERGE",FACE,{"derivedFrom":[makeQuery(id+"F1.opExtrude","SWEPT_FACE",FACE,{"disambiguationData":[OSD([subQ0])]}),makeQuery(id+"F11.opExtrude","CAP_FACE",FACE,{"disambiguationData":[OSD([subQ0,sQuery(id+"F0.wireOp",EDGE,"E0.left"),sQuery(id+"F0.wireOp",EDGE,"E0.right"),sQuery(id+"F10.wireOp",EDGE,"E33"),sQuery(id+"F10.wireOp",EDGE,"E34"),sQuery(id+"F10.wireOp",EDGE,"E37"),sQuery(id+"F10.wireOp",EDGE,"E38")])],"isStart":true})]})});}
            var Q5;
            {var subQ0=sQuery(id+"F0.wireOp",EDGE,"E0.bottom");Q5=makeQuery(id+"F19.boolean.opBoolean","SPLIT",FACE,{"disambiguationData":[TD([makeQuery(id+"F19.opExtrude","SWEPT_FACE",FACE,{"disambiguationData":[OSD([sQuery(id+"F17.wireOp",EDGE,"E207.sketch_text.stroke-12")])]})])],"derivedFrom":makeQuery(id+"F11.boolean.opBoolean","MERGE",FACE,{"derivedFrom":[makeQuery(id+"F1.opExtrude","SWEPT_FACE",FACE,{"disambiguationData":[OSD([subQ0])]}),makeQuery(id+"F11.opExtrude","CAP_FACE",FACE,{"disambiguationData":[OSD([subQ0,sQuery(id+"F0.wireOp",EDGE,"E0.left"),sQuery(id+"F0.wireOp",EDGE,"E0.right"),sQuery(id+"F10.wireOp",EDGE,"E33"),sQuery(id+"F10.wireOp",EDGE,"E34"),sQuery(id+"F10.wireOp",EDGE,"E37"),sQuery(id+"F10.wireOp",EDGE,"E38")])],"isStart":true})]})});}
            var Q6;
            {var subQ0=sQuery(id+"F0.wireOp",EDGE,"E0.bottom");Q6=makeQuery(id+"F19.boolean.opBoolean","SPLIT",FACE,{"disambiguationData":[TD([makeQuery(id+"F19.opExtrude","SWEPT_FACE",FACE,{"disambiguationData":[OSD([sQuery(id+"F17.wireOp",EDGE,"E207.sketch_text.stroke-79")])]})])],"derivedFrom":makeQuery(id+"F11.boolean.opBoolean","MERGE",FACE,{"derivedFrom":[makeQuery(id+"F1.opExtrude","SWEPT_FACE",FACE,{"disambiguationData":[OSD([subQ0])]}),makeQuery(id+"F11.opExtrude","CAP_FACE",FACE,{"disambiguationData":[OSD([subQ0,sQuery(id+"F0.wireOp",EDGE,"E0.left"),sQuery(id+"F0.wireOp",EDGE,"E0.right"),sQuery(id+"F10.wireOp",EDGE,"E33"),sQuery(id+"F10.wireOp",EDGE,"E34"),sQuery(id+"F10.wireOp",EDGE,"E37"),sQuery(id+"F10.wireOp",EDGE,"E38")])],"isStart":true})]})});}
            var Q7;
            {var subQ0=sQuery(id+"F12.wireOp",EDGE,"E196");var subQ1=sQuery(id+"F12.wireOp",EDGE,"E177.MirrorCS");var subQ2=sQuery(id+"F12.wireOp",EDGE,"E168.MirrorCS");Q7=makeQuery(id+"F16.boolean.opBoolean","MERGE",EDGE,{"derivedFrom":[makeQuery(id+"F13.boolean.opBoolean","COPY",EDGE,{"derivedFrom":makeQuery(id+"F13.opExtrude","SWEPT_EDGE",EDGE,{"disambiguationData":[OSD([subQ2,subQ1,subQ0])]})}),makeQuery(id+"F16.opExtrude","SWEPT_EDGE",EDGE,{"disambiguationData":[OSD([subQ2,subQ1,subQ0])]})]});}
            var Q8;
            {var subQ0=sQuery(id+"F12.wireOp",EDGE,"E196");var subQ1=sQuery(id+"F12.wireOp",EDGE,"E178.MirrorCS");var subQ2=sQuery(id+"F12.wireOp",EDGE,"E173.MirrorCS");Q8=makeQuery(id+"F16.boolean.opBoolean","MERGE",EDGE,{"derivedFrom":[makeQuery(id+"F13.boolean.opBoolean","COPY",EDGE,{"derivedFrom":makeQuery(id+"F13.opExtrude","SWEPT_EDGE",EDGE,{"disambiguationData":[OSD([subQ2,subQ1,subQ0])]})}),makeQuery(id+"F16.opExtrude","SWEPT_EDGE",EDGE,{"disambiguationData":[OSD([subQ2,subQ1,subQ0])]})]});}
            var Q9;
            {var subQ0=sQuery(id+"F12.wireOp",EDGE,"E198");var subQ1=sQuery(id+"F12.wireOp",EDGE,"E80.MirrorCS");var subQ2=sQuery(id+"F12.wireOp",EDGE,"E78.MirrorCS");Q9=makeQuery(id+"F16.boolean.opBoolean","MERGE",EDGE,{"derivedFrom":[makeQuery(id+"F13.boolean.opBoolean","COPY",EDGE,{"derivedFrom":makeQuery(id+"F13.opExtrude","SWEPT_EDGE",EDGE,{"disambiguationData":[OSD([subQ2,subQ1,subQ0])]})}),makeQuery(id+"F16.opExtrude","SWEPT_EDGE",EDGE,{"disambiguationData":[OSD([subQ2,subQ1,subQ0])]})]});}
            var Q10;
            {var subQ0=sQuery(id+"F12.wireOp",EDGE,"E198");var subQ1=sQuery(id+"F12.wireOp",EDGE,"E82.MirrorCS");var subQ2=sQuery(id+"F12.wireOp",EDGE,"E77.MirrorCS");Q10=makeQuery(id+"F16.boolean.opBoolean","MERGE",EDGE,{"derivedFrom":[makeQuery(id+"F13.boolean.opBoolean","COPY",EDGE,{"derivedFrom":makeQuery(id+"F13.opExtrude","SWEPT_EDGE",EDGE,{"disambiguationData":[OSD([subQ2,subQ1,subQ0])]})}),makeQuery(id+"F16.opExtrude","SWEPT_EDGE",EDGE,{"disambiguationData":[OSD([subQ2,subQ1,subQ0])]})]});}
            var Q11;
            {var subQ0=sQuery(id+"F12.wireOp",EDGE,"E199");var subQ1=sQuery(id+"F12.wireOp",EDGE,"E65");var subQ2=sQuery(id+"F12.wireOp",EDGE,"E64");Q11=makeQuery(id+"F16.boolean.opBoolean","MERGE",EDGE,{"derivedFrom":[makeQuery(id+"F13.boolean.opBoolean","COPY",EDGE,{"derivedFrom":makeQuery(id+"F13.opExtrude","SWEPT_EDGE",EDGE,{"disambiguationData":[OSD([subQ2,subQ1,subQ0])]})}),makeQuery(id+"F16.opExtrude","SWEPT_EDGE",EDGE,{"disambiguationData":[OSD([subQ2,subQ1,subQ0])]})]});}
            var Q12;
            {var subQ0=sQuery(id+"F12.wireOp",EDGE,"E199");var subQ1=sQuery(id+"F12.wireOp",EDGE,"E73.trimOffspring");var subQ2=sQuery(id+"F12.wireOp",EDGE,"E68");Q12=makeQuery(id+"F16.boolean.opBoolean","MERGE",EDGE,{"derivedFrom":[makeQuery(id+"F13.boolean.opBoolean","COPY",EDGE,{"derivedFrom":makeQuery(id+"F13.opExtrude","SWEPT_EDGE",EDGE,{"disambiguationData":[OSD([subQ2,subQ1,subQ0])]})}),makeQuery(id+"F16.opExtrude","SWEPT_EDGE",EDGE,{"disambiguationData":[OSD([subQ2,subQ1,subQ0])]})]});}
            var Q13;
            {var subQ0=sQuery(id+"F12.wireOp",EDGE,"E197");var subQ1=sQuery(id+"F12.wireOp",EDGE,"E176.MirrorCS");var subQ2=sQuery(id+"F12.wireOp",EDGE,"E172.MirrorCS");Q13=makeQuery(id+"F16.boolean.opBoolean","MERGE",EDGE,{"derivedFrom":[makeQuery(id+"F13.boolean.opBoolean","COPY",EDGE,{"derivedFrom":makeQuery(id+"F13.opExtrude","SWEPT_EDGE",EDGE,{"disambiguationData":[OSD([subQ2,subQ1,subQ0])]})}),makeQuery(id+"F16.opExtrude","SWEPT_EDGE",EDGE,{"disambiguationData":[OSD([subQ2,subQ1,subQ0])]})]});}
            var Q14;
            {var subQ0=sQuery(id+"F12.wireOp",EDGE,"E197");var subQ1=sQuery(id+"F12.wireOp",EDGE,"E175.MirrorCS");var subQ2=sQuery(id+"F12.wireOp",EDGE,"E167.MirrorCS");Q14=makeQuery(id+"F16.boolean.opBoolean","MERGE",EDGE,{"derivedFrom":[makeQuery(id+"F13.boolean.opBoolean","COPY",EDGE,{"derivedFrom":makeQuery(id+"F13.opExtrude","SWEPT_EDGE",EDGE,{"disambiguationData":[OSD([subQ2,subQ1,subQ0])]})}),makeQuery(id+"F16.opExtrude","SWEPT_EDGE",EDGE,{"disambiguationData":[OSD([subQ2,subQ1,subQ0])]})]});}
            fillet(context, id + "F20", {"entities" : qUnion([Q0, Q1, Q2, Q3, Q4, Q5, Q6, Q7, Q8, Q9, Q10, Q11, Q12, Q13, Q14]), "radius" : .1 * mm, "tangentPropagation" : true, "allowEdgeOverflow" : false});
        }
    });
